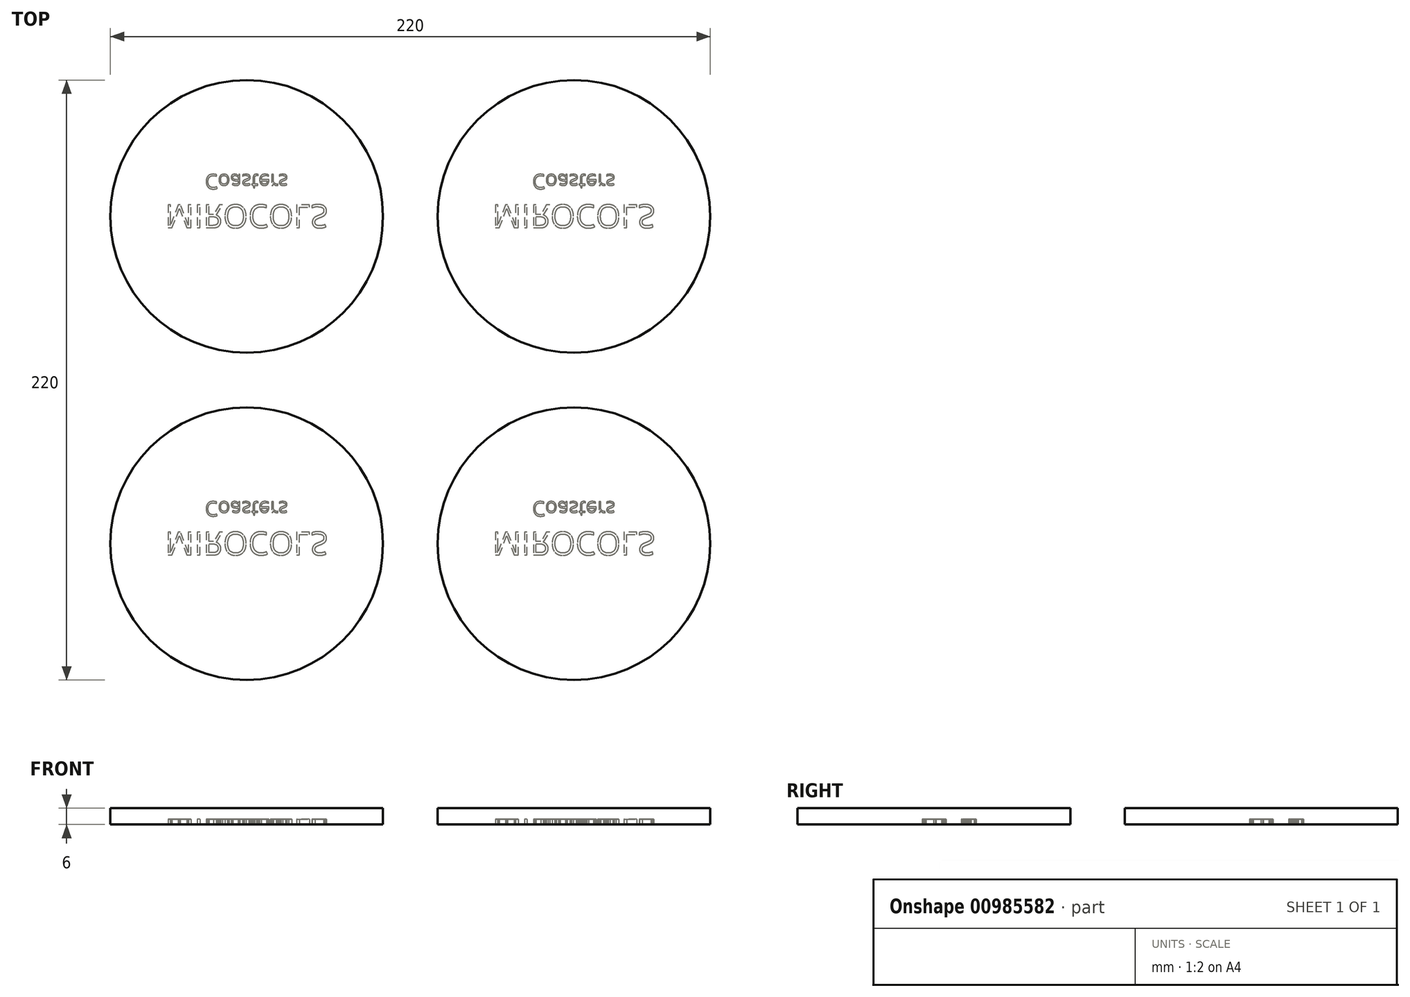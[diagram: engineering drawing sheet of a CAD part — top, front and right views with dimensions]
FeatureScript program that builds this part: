
annotation { "Feature Type Name" : "Feature", "Feature Type Description" : "" }
export const myFeature = defineFeature(function(context is Context, id is Id, definition is map)
    precondition{}
    {
        {
            var Q0;
            Q0=qCreatedBy(makeId("Top.planeOp"),FACE);
            var sketch = newSketch(context, id + "F0", { "sketchPlane" : qUnion([Q0])});
            skCircle(sketch, "E0", {"center": v(0, 0) * mm, "radius": 50 * mm});
            skSolve(sketch);
        }
        {
            var Q0;
            Q0=makeQuery(id+"F0.imprint","IMPRINT",FACE,{"disambiguationData":[TD([[makeQuery(id+"F0.imprint","IMPRINT",EDGE,{"derivedFrom":sQuery(id+"F0.wireOp",EDGE,"E0")}),1.0]])]});
            extrude(context, id + "F1", {"entities" : qUnion([Q0]), "depth" : 6 * mm, "offsetDistance" : 25 * mm});
        }
        {
            var Q0;
            Q0=makeQuery(id+"F1.opExtrude","CAP_FACE",FACE,{"disambiguationData":[OSD([sQuery(id+"F0.wireOp",EDGE,"E0")])],"isStart":true});
            var sketch = newSketch(context, id + "F2", { "sketchPlane" : qUnion([Q0])});
            skText(sketch, "E1", { "text": "MIROCOLS", "fontName": "OpenSans-Regular.ttf"});
            const initialGuessF2  = {"E1": [-0.03, -0.00427, 1, 0, 0.00852]};
            skSetInitialGuess(sketch, initialGuessF2);
            skSolve(sketch);
        }
        {
            var Q0;
            Q0 = qSketchRegion(id + "F2", true);
            extrude(context, id + "F3", {"entities" : qUnion([Q0]), "operationType" : NewBodyOperationType.REMOVE, "oppositeDirection" : true, "depth" : 2 * mm, "offsetDistance" : 25 * mm});
        }
        {
            var Q0;
            {var subQ0=sQuery(id+"F0.wireOp",EDGE,"E0");Q0=makeQuery(id+"F3.boolean.opBoolean","SPLIT",FACE,{"disambiguationData":[TD([makeQuery(id+"F1.opExtrude","SWEPT_FACE",FACE,{"disambiguationData":[OSD([subQ0])]})])],"derivedFrom":makeQuery(id+"F1.opExtrude","CAP_FACE",FACE,{"disambiguationData":[OSD([subQ0])],"isStart":true})});}
            var sketch = newSketch(context, id + "F4", { "sketchPlane" : qUnion([Q0])});
            skText(sketch, "E2", { "text": "Coasters", "fontName": "OpenSans-Regular.ttf"});
            const initialGuessF4  = {"E2": [-0.0153, -0.01542, 1, 0, 0.00539]};
            skSetInitialGuess(sketch, initialGuessF4);
            skSolve(sketch);
        }
        {
            var Q0;
            Q0 = qSketchRegion(id + "F4", true);
            extrude(context, id + "F5", {"entities" : qUnion([Q0]), "operationType" : NewBodyOperationType.REMOVE, "oppositeDirection" : true, "depth" : 2 * mm, "offsetDistance" : 25 * mm});
        }
        {
            var Q0;
            Q0=makeQuery(id+"F1.opExtrude","SWEPT_BODY",BODY,{"disambiguationData":[OSD([sQuery(id+"F0.wireOp",EDGE,"E0")])]});
            transform(context, id + "F6", {"entities" : qUnion([Q0]), "transformType" : TransformType.TRANSLATION_3D, "dx" : 120 * mm, "dy" : 0 * mm, "dz" : 0 * mm, "makeCopy" : true});
        }
        {
            var Q0;
            Q0=makeQuery(id+"F1.opExtrude","SWEPT_BODY",BODY,{"disambiguationData":[OSD([sQuery(id+"F0.wireOp",EDGE,"E0")])]});
            transform(context, id + "F7", {"entities" : qUnion([Q0]), "transformType" : TransformType.TRANSLATION_3D, "dx" : 0 * mm, "dy" : 120 * mm, "dz" : 0 * mm, "makeCopy" : true});
        }
        {
            var Q0;
            Q0=makeQuery(id+"F6.opPattern","COPY",BODY,{"derivedFrom":makeQuery(id+"F1.opExtrude","SWEPT_BODY",BODY,{"disambiguationData":[OSD([sQuery(id+"F0.wireOp",EDGE,"E0")])]}),"instanceName":"1"});
            transform(context, id + "F8", {"entities" : qUnion([Q0]), "transformType" : TransformType.TRANSLATION_3D, "dx" : 0 * mm, "dy" : 120 * mm, "dz" : 0 * mm, "makeCopy" : true});
        }
    });
